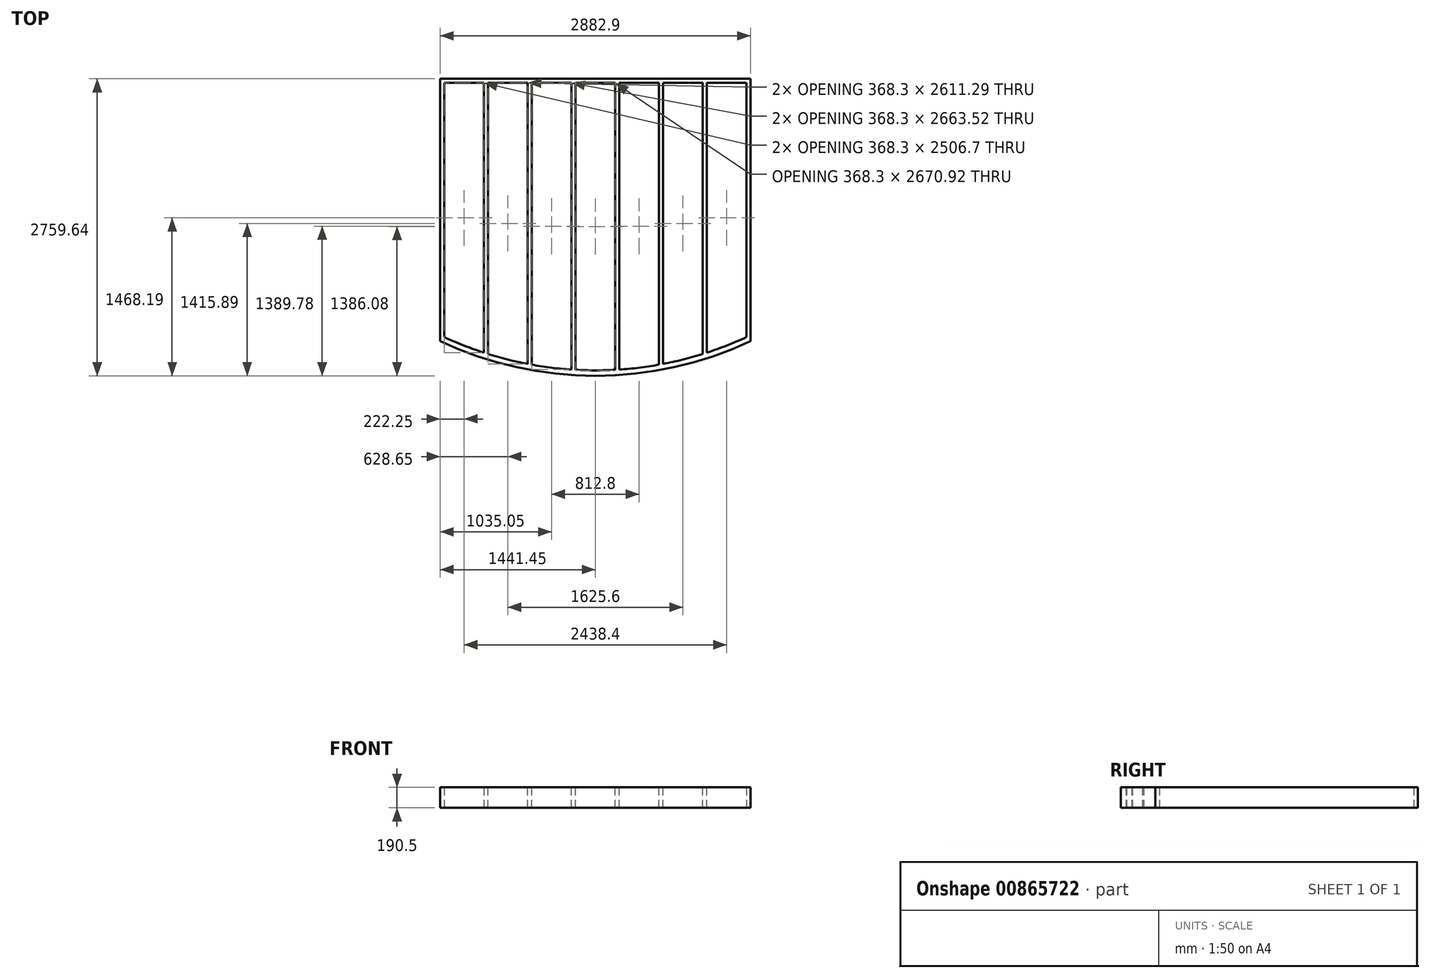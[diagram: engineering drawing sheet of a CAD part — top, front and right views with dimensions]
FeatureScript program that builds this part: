
annotation { "Feature Type Name" : "Feature", "Feature Type Description" : "" }
export const myFeature = defineFeature(function(context is Context, id is Id, definition is map)
    precondition{}
    {
        {
            var Q0;
            Q0=qCreatedBy(makeId("Right.planeOp"),FACE);
            var sketch = newSketch(context, id + "F0", { "sketchPlane" : qUnion([Q0])});
            skLineSegment(sketch, "E0.bottom", {"start": v(0, 0) * mm, "end": v(-38.1, 0) * mm});
            skLineSegment(sketch, "E0.top", {"start": v(0, 190.5) * mm, "end": v(-38.1, 190.5) * mm});
            skLineSegment(sketch, "E0.left", {"start": v(0, 0) * mm, "end": v(0, 190.5) * mm});
            skLineSegment(sketch, "E0.right", {"start": v(-38.1, 0) * mm, "end": v(-38.1, 190.5) * mm});
            skSolve(sketch);
        }
        {
            var Q0;
            Q0=makeQuery(id+"F0.imprint","IMPRINT",FACE,{"disambiguationData":[TD([[makeQuery(id+"F0.imprint","IMPRINT",EDGE,{"derivedFrom":sQuery(id+"F0.wireOp",EDGE,"E0.bottom")}),-1.0]])]});
            extrude(context, id + "F1", {"entities" : qUnion([Q0]), "oppositeDirection" : true, "depth" : 2882.9 * mm, "offsetDistance" : 25.4 * mm});
        }
        {
            var Q0;
            Q0=makeQuery(id+"F1.opExtrude","SWEPT_FACE",FACE,{"disambiguationData":[OSD([sQuery(id+"F0.wireOp",EDGE,"E0.right")])]});
            var sketch = newSketch(context, id + "F2", { "sketchPlane" : qUnion([Q0])});
            skLineSegment(sketch, "E1.bottom", {"start": v(0, 190.5) * mm, "end": v(-38.1, 190.5) * mm});
            skLineSegment(sketch, "E1.top", {"start": v(0, 0) * mm, "end": v(-38.1, 0) * mm});
            skLineSegment(sketch, "E1.left", {"start": v(0, 190.5) * mm, "end": v(0, 0) * mm});
            skLineSegment(sketch, "E1.right", {"start": v(-38.1, 190.5) * mm, "end": v(-38.1, 0) * mm});
            skSolve(sketch);
        }
        {
            var Q0;
            Q0 = qSketchRegion(id + "F2", true);
            extrude(context, id + "F3", {"entities" : qUnion([Q0]), "operationType" : NewBodyOperationType.ADD, "depth" : 2362.2 * mm, "offsetDistance" : 25.4 * mm});
        }
        {
            var Q0;
            Q0=makeQuery(id+"F1.opExtrude","SWEPT_FACE",FACE,{"disambiguationData":[OSD([sQuery(id+"F0.wireOp",EDGE,"E0.right")])]});
            var sketch = newSketch(context, id + "F4", { "sketchPlane" : qUnion([Q0])});
            skLineSegment(sketch, "E2.bottom", {"start": v(-2882.9, 190.5) * mm, "end": v(-2844.8, 190.5) * mm});
            skLineSegment(sketch, "E2.top", {"start": v(-2882.9, 0) * mm, "end": v(-2844.8, 0) * mm});
            skLineSegment(sketch, "E2.left", {"start": v(-2882.9, 190.5) * mm, "end": v(-2882.9, 0) * mm});
            skLineSegment(sketch, "E2.right", {"start": v(-2844.8, 190.5) * mm, "end": v(-2844.8, 0) * mm});
            skSolve(sketch);
        }
        {
            var Q0;
            Q0 = qSketchRegion(id + "F4", true);
            var Q1;
            Q1=makeQuery(id+"F3.opExtrude","CAP_FACE",FACE,{"disambiguationData":[OSD([sQuery(id+"F2.wireOp",EDGE,"E1.bottom"),sQuery(id+"F2.wireOp",EDGE,"E1.top"),sQuery(id+"F2.wireOp",EDGE,"E1.left"),sQuery(id+"F2.wireOp",EDGE,"E1.right")])],"isStart":false});
            extrude(context, id + "F5", {"entities" : qUnion([Q0]), "operationType" : NewBodyOperationType.ADD, "endBound" : BoundingType.UP_TO_SURFACE, "depth" : 25.4 * mm, "endBoundEntityFace" : qUnion([Q1]), "offsetDistance" : 25.4 * mm});
        }
        {
            var Q0;
            Q0=makeQuery(id+"F5.boolean.opBoolean","MERGE",FACE,{"derivedFrom":[makeQuery(id+"F3.boolean.opBoolean","MERGE",FACE,{"derivedFrom":[makeQuery(id+"F1.opExtrude","SWEPT_FACE",FACE,{"disambiguationData":[OSD([sQuery(id+"F0.wireOp",EDGE,"E0.top")])]}),makeQuery(id+"F3.opExtrude","SWEPT_FACE",FACE,{"disambiguationData":[OSD([sQuery(id+"F2.wireOp",EDGE,"E1.bottom")])]})]}),makeQuery(id+"F5.opExtrude","SWEPT_FACE",FACE,{"disambiguationData":[OSD([sQuery(id+"F4.wireOp",EDGE,"E2.bottom")])]})]});
            var sketch = newSketch(context, id + "F6", { "sketchPlane" : qUnion([Q0])});
            skLineSegment(sketch, "E3", {"start": v(-2882.9, -2400.3) * mm, "end": v(-2882.9, -2438.4) * mm});
            skLineSegment(sketch, "E4", {"start": v(0, -2400.3) * mm, "end": v(0, -2438.4) * mm});
            skArc(sketch, "E5", {"start": v(-2882.9, -2438.4) * mm, "mid": v(-1441.45, -2759.64) * mm, "end": v(0, -2438.4) * mm});
            skArc(sketch, "E6", {"start": v(-2844.8, -2400.3) * mm, "mid": v(-1441.45, -2709.02) * mm, "end": v(-38.1, -2400.3) * mm});
            skSolve(sketch);
        }
        {
            var Q0;
            {var subQ1=sQuery(id+"F6.wireOp",EDGE,"E3");Q0=makeQuery(id+"F6.imprint","IMPRINT",FACE,{"disambiguationData":[TD([[makeQuery(id+"F6.imprint","IMPRINT",EDGE,{"derivedFrom":subQ1}),1.0]])]});}
            var Q1;
            Q1=makeQuery(id+"F5.boolean.opBoolean","MERGE",FACE,{"derivedFrom":[makeQuery(id+"F3.boolean.opBoolean","MERGE",FACE,{"derivedFrom":[makeQuery(id+"F1.opExtrude","SWEPT_FACE",FACE,{"disambiguationData":[OSD([sQuery(id+"F0.wireOp",EDGE,"E0.bottom")])]}),makeQuery(id+"F3.opExtrude","SWEPT_FACE",FACE,{"disambiguationData":[OSD([sQuery(id+"F2.wireOp",EDGE,"E1.top")])]})]}),makeQuery(id+"F5.opExtrude","SWEPT_FACE",FACE,{"disambiguationData":[OSD([sQuery(id+"F4.wireOp",EDGE,"E2.top")])]})]});
            extrude(context, id + "F7", {"entities" : qUnion([Q0]), "endBound" : BoundingType.UP_TO_SURFACE, "oppositeDirection" : true, "depth" : 25.4 * mm, "endBoundEntityFace" : qUnion([Q1]), "offsetDistance" : 25.4 * mm});
        }
        {
            var Q0;
            Q0=makeQuery(id+"F1.opExtrude","SWEPT_BODY",BODY,{"disambiguationData":[OSD([sQuery(id+"F0.wireOp",EDGE,"E0.bottom"),sQuery(id+"F0.wireOp",EDGE,"E0.top"),sQuery(id+"F0.wireOp",EDGE,"E0.left"),sQuery(id+"F0.wireOp",EDGE,"E0.right")])]});
            var Q1;
            Q1=makeQuery(id+"F7.opExtrude","SWEPT_BODY",BODY,{"disambiguationData":[OSD([sQuery(id+"F2.wireOp",EDGE,"E1.bottom"),sQuery(id+"F4.wireOp",EDGE,"E2.bottom"),sQuery(id+"F6.wireOp",EDGE,"E3"),sQuery(id+"F6.wireOp",EDGE,"E4"),sQuery(id+"F6.wireOp",EDGE,"E5"),sQuery(id+"F6.wireOp",EDGE,"E6")])]});
            booleanBodies(context, id + "F8", {"operationType" : BooleanOperationType.UNION, "tools" : qUnion([Q0, Q1])});
        }
        {
            var Q0;
            Q0=makeQuery(id+"F1.opExtrude","SWEPT_FACE",FACE,{"disambiguationData":[OSD([sQuery(id+"F0.wireOp",EDGE,"E0.right")])]});
            var sketch = newSketch(context, id + "F9", { "sketchPlane" : qUnion([Q0])});
            skLineSegment(sketch, "E7.bottom", {"start": v(-444.5, 190.5) * mm, "end": v(-406.4, 190.5) * mm});
            skLineSegment(sketch, "E7.top", {"start": v(-444.5, 0) * mm, "end": v(-406.4, 0) * mm});
            skLineSegment(sketch, "E7.left", {"start": v(-444.5, 190.5) * mm, "end": v(-444.5, 0) * mm});
            skLineSegment(sketch, "E7.right", {"start": v(-406.4, 190.5) * mm, "end": v(-406.4, 0) * mm});
            skLineSegment(sketch, "E8.bottom", {"start": v(-850.9, 190.5) * mm, "end": v(-812.8, 190.5) * mm});
            skLineSegment(sketch, "E8.top", {"start": v(-850.9, 0) * mm, "end": v(-812.8, 0) * mm});
            skLineSegment(sketch, "E8.left", {"start": v(-850.9, 190.5) * mm, "end": v(-850.9, 0) * mm});
            skLineSegment(sketch, "E8.right", {"start": v(-812.8, 190.5) * mm, "end": v(-812.8, 0) * mm});
            skLineSegment(sketch, "E9.bottom", {"start": v(-1257.3, 190.5) * mm, "end": v(-1219.2, 190.5) * mm});
            skLineSegment(sketch, "E9.top", {"start": v(-1257.3, 0) * mm, "end": v(-1219.2, 0) * mm});
            skLineSegment(sketch, "E9.left", {"start": v(-1257.3, 190.5) * mm, "end": v(-1257.3, 0) * mm});
            skLineSegment(sketch, "E9.right", {"start": v(-1219.2, 190.5) * mm, "end": v(-1219.2, 0) * mm});
            skLineSegment(sketch, "E10.bottom", {"start": v(-1663.7, 190.5) * mm, "end": v(-1625.6, 190.5) * mm});
            skLineSegment(sketch, "E10.top", {"start": v(-1663.7, 0) * mm, "end": v(-1625.6, 0) * mm});
            skLineSegment(sketch, "E10.left", {"start": v(-1663.7, 190.5) * mm, "end": v(-1663.7, 0) * mm});
            skLineSegment(sketch, "E10.right", {"start": v(-1625.6, 190.5) * mm, "end": v(-1625.6, 0) * mm});
            skLineSegment(sketch, "E11.bottom", {"start": v(-2070.1, 190.5) * mm, "end": v(-2032, 190.5) * mm});
            skLineSegment(sketch, "E11.top", {"start": v(-2070.1, 0) * mm, "end": v(-2032, 0) * mm});
            skLineSegment(sketch, "E11.left", {"start": v(-2070.1, 190.5) * mm, "end": v(-2070.1, 0) * mm});
            skLineSegment(sketch, "E11.right", {"start": v(-2032, 190.5) * mm, "end": v(-2032, 0) * mm});
            skLineSegment(sketch, "E12.bottom", {"start": v(-2476.5, 190.5) * mm, "end": v(-2438.4, 190.5) * mm});
            skLineSegment(sketch, "E12.top", {"start": v(-2476.5, 0) * mm, "end": v(-2438.4, 0) * mm});
            skLineSegment(sketch, "E12.left", {"start": v(-2476.5, 190.5) * mm, "end": v(-2476.5, 0) * mm});
            skLineSegment(sketch, "E12.right", {"start": v(-2438.4, 190.5) * mm, "end": v(-2438.4, 0) * mm});
            skSolve(sketch);
        }
        {
            var Q0;
            Q0 = qSketchRegion(id + "F9", true);
            extrude(context, id + "F10", {"entities" : qUnion([Q0]), "operationType" : NewBodyOperationType.ADD, "endBound" : BoundingType.UP_TO_NEXT, "depth" : 25.4 * mm, "offsetDistance" : 25.4 * mm});
        }
    });
